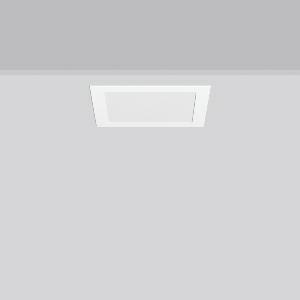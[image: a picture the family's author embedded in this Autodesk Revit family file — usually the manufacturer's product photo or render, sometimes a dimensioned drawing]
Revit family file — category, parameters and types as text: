
# Revit family: toledo_flat_square_e_901716_002_1_19_dd83
name_source: partatom
category: Lighting Fixtures
units: mm (PartAtom-declared; Revit-internal decimal feet)

## family parameters
Cut with Voids When Loaded = No
Host = Face
Light Source = No
Part Type = Normal
Room Calculation Point = No
Round Connector Dimension = Use Diameter
Shared = No

## types (1)
- TOLEDO FLAT square E (1 x LED Modul 840, 1800 lm, 4000)
    Apparent Load = 17 VA
    CIE Flux Codes = 49 80 96 100 100
    Color Rendering = 80
    Color Temperature = 4000
    Default Elevation = 1800 mm  [stored 5.90551 ft]
    Description = Series: TOLEDO FLAT square
Ultra thin recessed downlight. Housing: die-cast aluminium. Light guide and diffuser made of non-yellowing PMMA, opal matt. Ceiling installation with spring system. Mounting depth depends on ceiling strength. Including separate LED converter with connecting cable 250 mm.Connected HF motion detector in a separate ballast box.Adjustable dim functions Soft Start, Corridor, Permanent. Wireless networking, sensor configuration and communication via Bluetooth. Operation via an Android / iOS device, free app available for download. master/slave Brightness sensor without function. Not suitable for metal ceilings.Versions with movement sensor not suitable for surface-mounted housing. Suitable for through-wiring with separately available accessories. Retrofittable decorative cylinders made of chintz fabric as accessory, optional with satin finish plastic diffuser. Through-wiring box (5 pole) available as accessory. 
Colour: white
Length: 225 mm
Width: 225 mm
Height: 3 mm
Cut-out length: 208 mm
Cut-out width: 208 mm
Recess height: 55-76 mm
Luminaire: recess height: 31-51 mm
Lamp: LED
Socket: without socket
Colour temperature: 4000K
Colour rendering index (CRI): 80
System power: 17 W
Rated luminous flux: 1800 lm
Luminous efficiency: 106 lm/W
Control gear: Dimmable Bluetooth converter
Protection class: I
Type of protection: IP 54
    Height = 0 mm  [stored 0 ft]
    Lamp = 1 x LED Modul 840
    Lamp Light Flux = 1800 lm
    Lamp count = 1
    Length = 225 mm
    Lifetime = 50000 h
    Luminous efficacy = 106 lm/W
    Manufacturer = RZB
    ModVariant = No
    Model = 901716.002.1.19
    Mounting Place = Ceiling
    Mounting Type = Recessed
    Number of Poles = 1
    OnlyDefault = Yes
    Power Factor = 1
    Product Name = TOLEDO FLAT square E
    Product group = Recessed downlights
    ProductGroupID = 402
    Protection Class = Protection class I
    Protection Degree = IP 20
    RLX_Detail_Level = 1
    RLX_Emergency_Light_Flux = 0 lm
    RLX_Emergency_Type = 0
    RLX_Emergency_Type_DB = No
    RlxData = <blob elided: 11465 chars, md5=bb8b16f4>
    Socket = socket
    Standby Power = 0 W
    System Light Flux = 1800 lm
    System Power = 17 W
    Type Comments = Product without accessories
    Type Image = 901487.002.jpg
    URL = http://relux.com
    VarID = ---
    Voltage = 230 V
    Voltage Range = 220-240 V
    Weight = 0.00 kg
    Width = 225 mm

note: [stored X ft] marks values corroborated as IEEE doubles in the binary element streams (Revit-internal decimal feet)

## geometry (parser evidence)
native form markers: Sweep x9
no freeform markers — native parametric forms only
